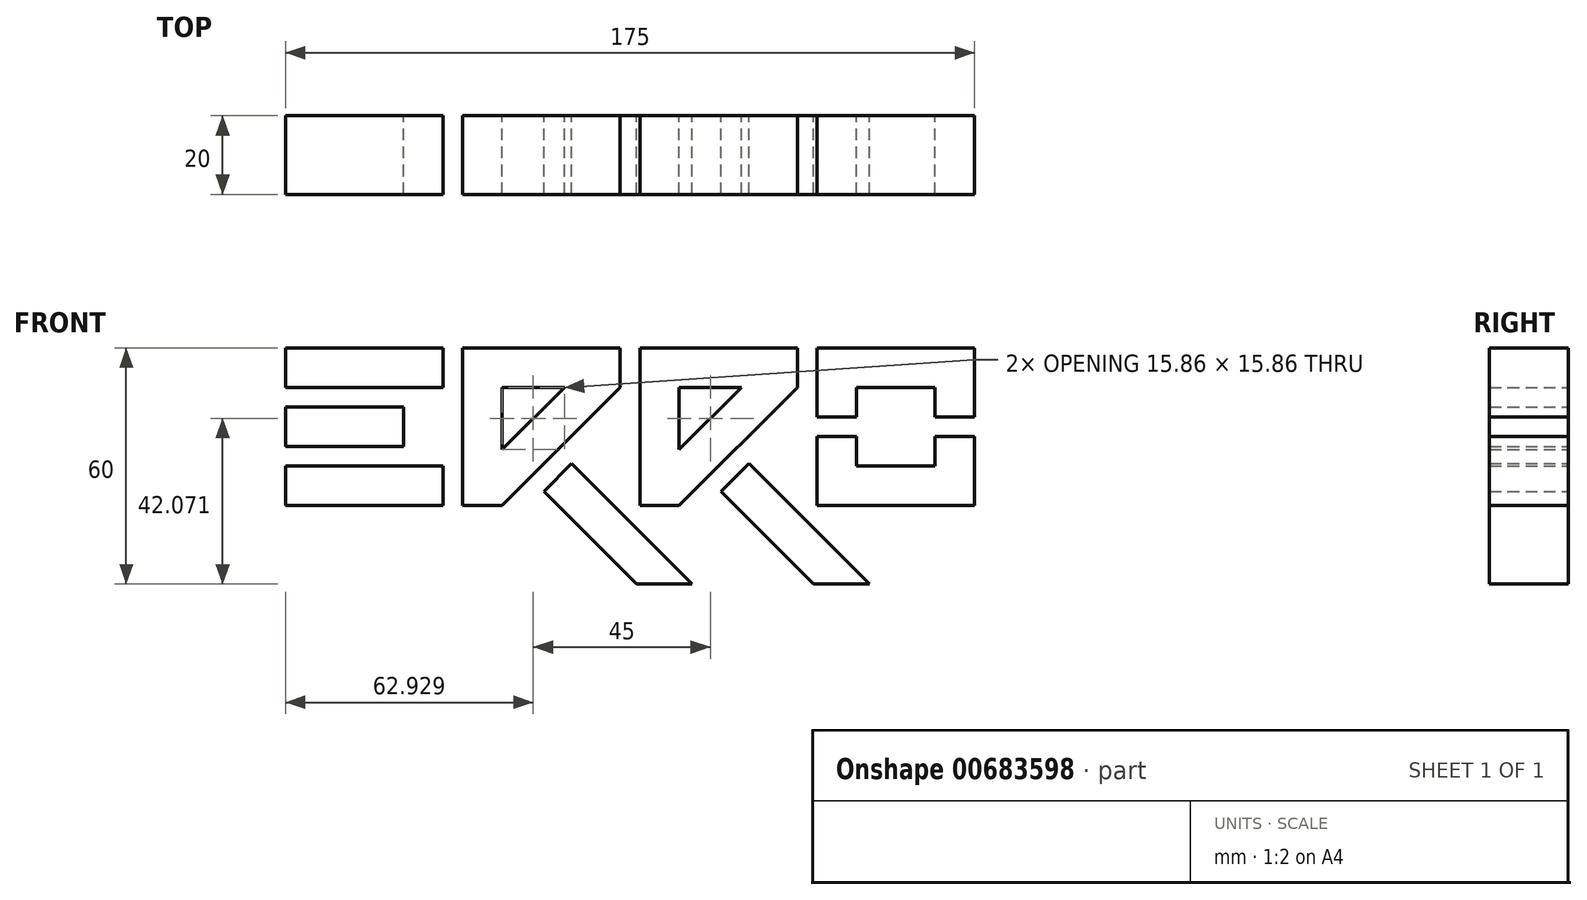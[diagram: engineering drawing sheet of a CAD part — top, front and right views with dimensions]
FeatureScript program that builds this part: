
annotation { "Feature Type Name" : "Feature", "Feature Type Description" : "" }
export const myFeature = defineFeature(function(context is Context, id is Id, definition is map)
    precondition{}
    {
        {
            var Q0;
            Q0=qCreatedBy(makeId("Front.planeOp"),FACE);
            var sketch = newSketch(context, id + "F0", { "sketchPlane" : qUnion([Q0])});
            skLineSegment(sketch, "E0.bottom", {"start": v(0, 0) * mm, "end": v(-40, 0) * mm});
            skLineSegment(sketch, "E0.top", {"start": v(0, 10) * mm, "end": v(-40, 10) * mm});
            skLineSegment(sketch, "E0.left", {"start": v(0, 0) * mm, "end": v(0, 10) * mm});
            skLineSegment(sketch, "E0.right", {"start": v(-40, 0) * mm, "end": v(-40, 10) * mm});
            skLineSegment(sketch, "E1.bottom", {"start": v(-40, 25) * mm, "end": v(-10, 25) * mm});
            skLineSegment(sketch, "E1.top", {"start": v(-40, 15) * mm, "end": v(-10, 15) * mm});
            skLineSegment(sketch, "E1.left", {"start": v(-40, 25) * mm, "end": v(-40, 15) * mm});
            skLineSegment(sketch, "E1.right", {"start": v(-10, 25) * mm, "end": v(-10, 15) * mm});
            skLineSegment(sketch, "E2.bottom", {"start": v(-40, 30) * mm, "end": v(0, 30) * mm});
            skLineSegment(sketch, "E2.top", {"start": v(-40, 40) * mm, "end": v(0, 40) * mm});
            skLineSegment(sketch, "E2.left", {"start": v(-40, 30) * mm, "end": v(-40, 40) * mm});
            skLineSegment(sketch, "E2.right", {"start": v(0, 30) * mm, "end": v(0, 40) * mm});
            skLineSegment(sketch, "E3", {"start": v(5, 0) * mm, "end": v(5, 40) * mm});
            skLineSegment(sketch, "E4", {"start": v(5, 40) * mm, "end": v(45, 40) * mm});
            skLineSegment(sketch, "E5", {"start": v(45, 40) * mm, "end": v(45, 30) * mm});
            skLineSegment(sketch, "E6", {"start": v(15, 0) * mm, "end": v(5, 0) * mm});
            skLineSegment(sketch, "E7", {"start": v(45, 30) * mm, "end": v(29.14, 14.14) * mm});
            skLineSegment(sketch, "E8", {"start": v(15, 0) * mm, "end": v(15, 0) * mm});
            skLineSegment(sketch, "E9", {"start": v(15, 30) * mm, "end": v(30.86, 30) * mm});
            skLineSegment(sketch, "E10", {"start": v(30.86, 30) * mm, "end": v(15, 14.14) * mm});
            skLineSegment(sketch, "E11", {"start": v(15, 14.14) * mm, "end": v(15, 30) * mm});
            skLineSegment(sketch, "E12", {"start": v(25.6, 3.54) * mm, "end": v(49.14, -20) * mm});
            skLineSegment(sketch, "E13", {"start": v(63.28, -20) * mm, "end": v(32.68, 10.6) * mm});
            skLineSegment(sketch, "E14", {"start": v(15, 14.14) * mm, "end": v(22.07, 7.07) * mm, "construction": true});
            skLineSegment(sketch, "E15.trimOffspring", {"start": v(22.07, 7.07) * mm, "end": v(15, 0) * mm});
            skLineSegment(sketch, "E16", {"start": v(50, 0) * mm, "end": v(50, 40) * mm});
            skLineSegment(sketch, "E17", {"start": v(50, 40) * mm, "end": v(90, 40) * mm});
            skLineSegment(sketch, "E18", {"start": v(90, 40) * mm, "end": v(90, 30) * mm});
            skLineSegment(sketch, "E19", {"start": v(60, 0) * mm, "end": v(50, 0) * mm});
            skLineSegment(sketch, "E20", {"start": v(90, 30) * mm, "end": v(74.14, 14.14) * mm});
            skLineSegment(sketch, "E21", {"start": v(60, 30) * mm, "end": v(75.86, 30) * mm});
            skLineSegment(sketch, "E22", {"start": v(75.86, 30) * mm, "end": v(60, 14.14) * mm});
            skLineSegment(sketch, "E23", {"start": v(60, 14.14) * mm, "end": v(60, 30) * mm});
            skLineSegment(sketch, "E24", {"start": v(70.6, 3.54) * mm, "end": v(94.14, -20) * mm});
            skLineSegment(sketch, "E25", {"start": v(108.28, -20) * mm, "end": v(77.68, 10.6) * mm});
            skLineSegment(sketch, "E26", {"start": v(60, 14.14) * mm, "end": v(67.07, 7.07) * mm, "construction": true});
            skLineSegment(sketch, "E27.trimOffspring", {"start": v(67.07, 7.07) * mm, "end": v(60, 0) * mm});
            skLineSegment(sketch, "E28.bottom", {"start": v(95, 0) * mm, "end": v(135, 0) * mm});
            skLineSegment(sketch, "E28.top", {"start": v(95, 40) * mm, "end": v(135, 40) * mm});
            skLineSegment(sketch, "E28.left", {"start": v(95, 0) * mm, "end": v(95, 17.5) * mm});
            skLineSegment(sketch, "E28.right", {"start": v(135, 0) * mm, "end": v(135, 17.5) * mm});
            skLineSegment(sketch, "E29.bottom", {"start": v(105, 30) * mm, "end": v(125, 30) * mm});
            skLineSegment(sketch, "E29.top", {"start": v(105, 10) * mm, "end": v(125, 10) * mm});
            skLineSegment(sketch, "E29.left", {"start": v(105, 30) * mm, "end": v(105, 22.5) * mm});
            skLineSegment(sketch, "E29.right", {"start": v(125, 30) * mm, "end": v(125, 22.5) * mm});
            skLineSegment(sketch, "E30", {"start": v(95, 17.5) * mm, "end": v(105, 17.5) * mm});
            skLineSegment(sketch, "E31", {"start": v(105, 22.5) * mm, "end": v(95, 22.5) * mm});
            skLineSegment(sketch, "E32", {"start": v(125, 22.5) * mm, "end": v(135, 22.5) * mm});
            skLineSegment(sketch, "E33", {"start": v(125, 17.5) * mm, "end": v(135, 17.5) * mm});
            skLineSegment(sketch, "E34.trimOffspring", {"start": v(95, 22.5) * mm, "end": v(95, 40) * mm});
            skLineSegment(sketch, "E35.trimOffspring", {"start": v(105, 17.5) * mm, "end": v(105, 10) * mm});
            skLineSegment(sketch, "E36.trimOffspring", {"start": v(125, 17.5) * mm, "end": v(125, 10) * mm});
            skLineSegment(sketch, "E37.trimOffspring", {"start": v(135, 22.5) * mm, "end": v(135, 40) * mm});
            skLineSegment(sketch, "E38", {"start": v(22.07, 7.07) * mm, "end": v(29.14, 14.14) * mm});
            skLineSegment(sketch, "E39", {"start": v(67.07, 7.07) * mm, "end": v(74.14, 14.14) * mm});
            skLineSegment(sketch, "E40", {"start": v(25.6, 3.54) * mm, "end": v(32.68, 10.6) * mm});
            skLineSegment(sketch, "E41", {"start": v(70.6, 3.54) * mm, "end": v(77.68, 10.6) * mm});
            skLineSegment(sketch, "E42", {"start": v(49.14, -20) * mm, "end": v(63.28, -20) * mm});
            skLineSegment(sketch, "E43.trimOffspring", {"start": v(94.14, -20) * mm, "end": v(108.28, -20) * mm});
            skSolve(sketch);
        }
        {
            var Q0;
            Q0=makeQuery(id+"F0.imprint","IMPRINT",FACE,{"disambiguationData":[TD([[makeQuery(id+"F0.imprint","IMPRINT",EDGE,{"derivedFrom":sQuery(id+"F0.wireOp",EDGE,"E1.bottom")}),-1.0]])]});
            var Q1;
            Q1=makeQuery(id+"F0.imprint","IMPRINT",FACE,{"disambiguationData":[TD([[makeQuery(id+"F0.imprint","IMPRINT",EDGE,{"derivedFrom":sQuery(id+"F0.wireOp",EDGE,"E2.bottom")}),1.0]])]});
            var Q2;
            Q2=makeQuery(id+"F0.imprint","IMPRINT",FACE,{"disambiguationData":[TD([[makeQuery(id+"F0.imprint","IMPRINT",EDGE,{"derivedFrom":sQuery(id+"F0.wireOp",EDGE,"E0.bottom")}),-1.0]])]});
            var Q3;
            Q3=makeQuery(id+"F0.imprint","IMPRINT",FACE,{"disambiguationData":[TD([[makeQuery(id+"F0.imprint","IMPRINT",EDGE,{"derivedFrom":sQuery(id+"F0.wireOp",EDGE,"E3")}),-1.0]])]});
            var Q4;
            Q4=makeQuery(id+"F0.imprint","IMPRINT",FACE,{"disambiguationData":[TD([[makeQuery(id+"F0.imprint","IMPRINT",EDGE,{"derivedFrom":sQuery(id+"F0.wireOp",EDGE,"E12")}),1.0]])]});
            var Q5;
            Q5=makeQuery(id+"F0.imprint","IMPRINT",FACE,{"disambiguationData":[TD([[makeQuery(id+"F0.imprint","IMPRINT",EDGE,{"derivedFrom":sQuery(id+"F0.wireOp",EDGE,"E24")}),1.0]])]});
            var Q6;
            Q6=makeQuery(id+"F0.imprint","IMPRINT",FACE,{"disambiguationData":[TD([[makeQuery(id+"F0.imprint","IMPRINT",EDGE,{"derivedFrom":sQuery(id+"F0.wireOp",EDGE,"E16")}),-1.0]])]});
            var Q7;
            Q7=makeQuery(id+"F0.imprint","IMPRINT",FACE,{"disambiguationData":[TD([[makeQuery(id+"F0.imprint","IMPRINT",EDGE,{"derivedFrom":sQuery(id+"F0.wireOp",EDGE,"E28.top")}),-1.0]])]});
            var Q8;
            Q8=makeQuery(id+"F0.imprint","IMPRINT",FACE,{"disambiguationData":[TD([[makeQuery(id+"F0.imprint","IMPRINT",EDGE,{"derivedFrom":sQuery(id+"F0.wireOp",EDGE,"E28.bottom")}),1.0]])]});
            extrude(context, id + "F1", {"entities" : qUnion([Q0, Q1, Q2, Q3, Q4, Q5, Q6, Q7, Q8]), "depth" : 20 * mm, "offsetDistance" : 25 * mm});
        }
    });
